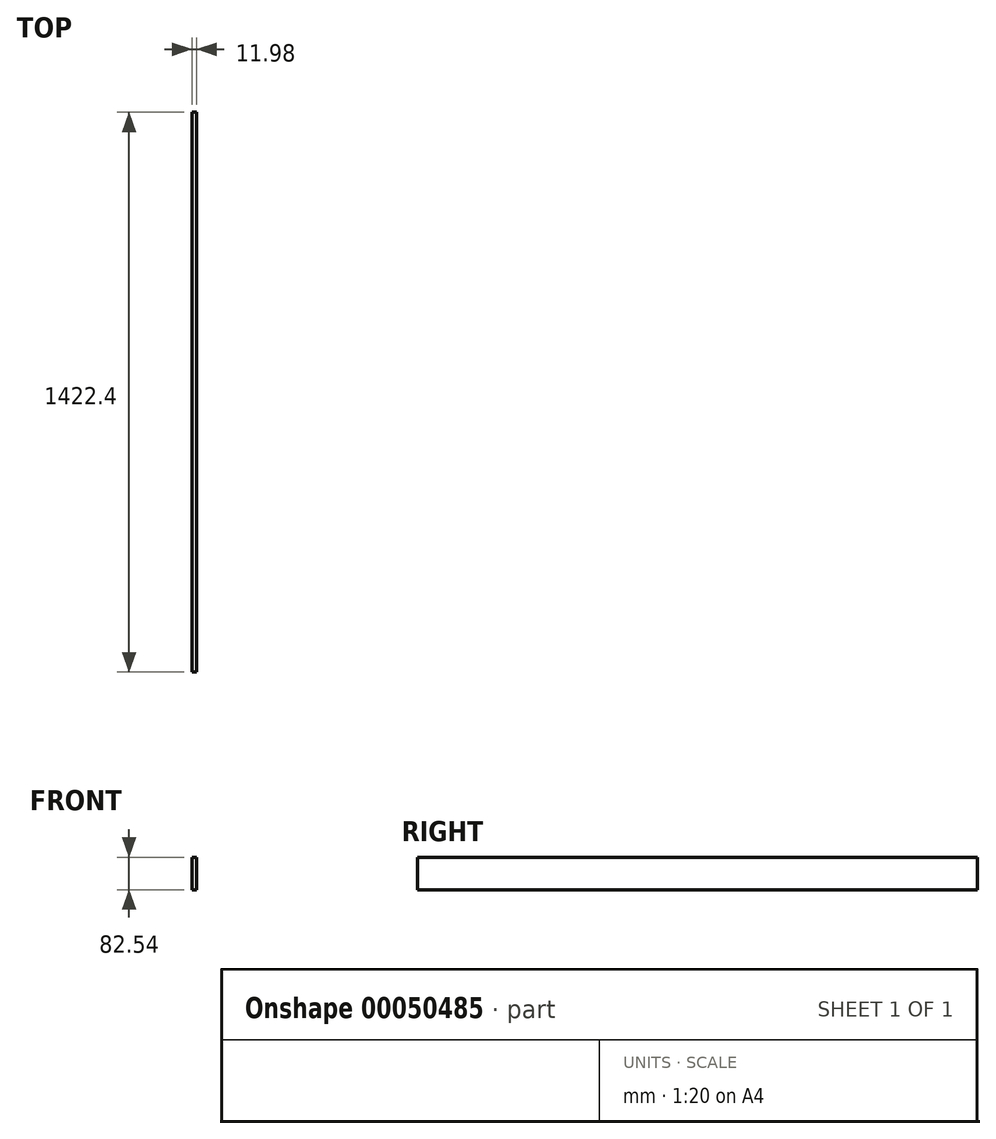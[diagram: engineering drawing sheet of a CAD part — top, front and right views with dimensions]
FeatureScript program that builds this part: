
annotation { "Feature Type Name" : "Feature", "Feature Type Description" : "" }
export const myFeature = defineFeature(function(context is Context, id is Id, definition is map)
    precondition{}
    {
        {
            var Q0;
            Q0=qCreatedBy(makeId("Right.planeOp"),FACE);
            var sketch = newSketch(context, id + "F0", { "sketchPlane" : qUnion([Q0])});
            skLineSegment(sketch, "E0.rect.bottom", {"start": v(711.2, -41.27) * mm, "end": v(-711.2, -41.28) * mm});
            skLineSegment(sketch, "E0.rect.top", {"start": v(711.2, 41.28) * mm, "end": v(-711.2, 41.27) * mm});
            skLineSegment(sketch, "E0.rect.left", {"start": v(711.2, -41.27) * mm, "end": v(711.2, 41.28) * mm});
            skLineSegment(sketch, "E0.rect.right", {"start": v(-711.2, -41.28) * mm, "end": v(-711.2, 41.27) * mm});
            skPoint(sketch, "E0.rect.middle", {"position": v(0, 0) * mm});
            skSolve(sketch);
        }
        {
            var Q0;
            Q0=qSketchRegion(id+"F0",true);
            extrude(context, id + "F1", {"entities" : qUnion([Q0]), "endBound" : BoundingType.SYMMETRIC, "depth" : 12 * mm});
        }
    });
